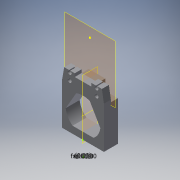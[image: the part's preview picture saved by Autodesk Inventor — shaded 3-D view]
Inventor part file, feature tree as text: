
AUTODESK INVENTOR PART (.ipt)
format: ipt  version: 2019.4 (Build 234330000, 330)  size: 620,032 bytes
history: native  units: mm
features: other x7, reference x6, extrude x5, sketch x5, plane x2, projected_geometry x2, helix x1
ambient origin geometry x8: Origin, YZ Plane, XZ Plane, XY Plane, X Axis, Y Axis, Z Axis, Center Point
bodies: Solid1 (feature_tree)
feature tree (28):
  plane  "Work Plane1"
  extrude  "Extrusion1"  Depth=30.0mm
  extrude  "Extrusion2"  Depth=5.0mm TaperAngle=0.0deg
  extrude  "Extrusion4"  Depth=5.0mm TaperAngle=0.0deg
  extrude  "Extrusion5"  Depth=1.0mm TaperAngle=0.0deg
  extrude  "Extrusion6"  Depth=9.95mm
  plane  "Work Plane2"
  other  "Work Axis2"
  helix  "Coil1"  [1 undecoded]
  sketch  "Sketch1"  dims[d0=25.0mm d1=30.0mm]
  reference  "Reference1"
  reference  "Reference2"
  sketch  "Sketch2"  dims[d2=30.0mm d3=5.0mm d4=0.0mm]
  reference  "Reference3"
  reference  "Reference4"
  reference  "Reference5"
  projected_geometry  "Projected Loop1"
  sketch  "Sketch4"  dims[d5=21.0mm d6=5.0mm d7=0.0mm]
  sketch  "Sketch5"  dims[d10=5.0mm d11=0.0mm d12=1.0mm d13=0.0mm]
  projected_geometry  "Projected Loop2"
  sketch  "Sketch6"  dims[d14=1.0mm d15=0.0mm d16=0.15mm d17=0.0mm d18=120.0deg d19=0.15mm d20=120.0deg d21=1.0mm d22=0.713333mm d25=0.713333mm d26=10.0mm d27=130.0mm d28=0.0mm d29=90.0deg d30=90.0deg d31=0.0mm d32=0.0mm d33=9.95mm]
  reference  "Reference7"
  other  "Assembly_Cube_Z_Focus_MGN_NEMA_v3.iam"
  other  "30_Cube_Z_Focus_MGN_NEMA_slide:1"
  other  "00_Microscope_Objective_Lens10x:1"
  other  "Assembly_Cube_empty_IM_v3:2"
  other  "10_Cube_1x1_IM:1"
  other  "00_RMS_Thread:1"
note: 1 required parameter value undecoded (feature->parameter linkage not recoverable at this tier; creation-order binding heuristic only, values carry confidence <= 0.55)
